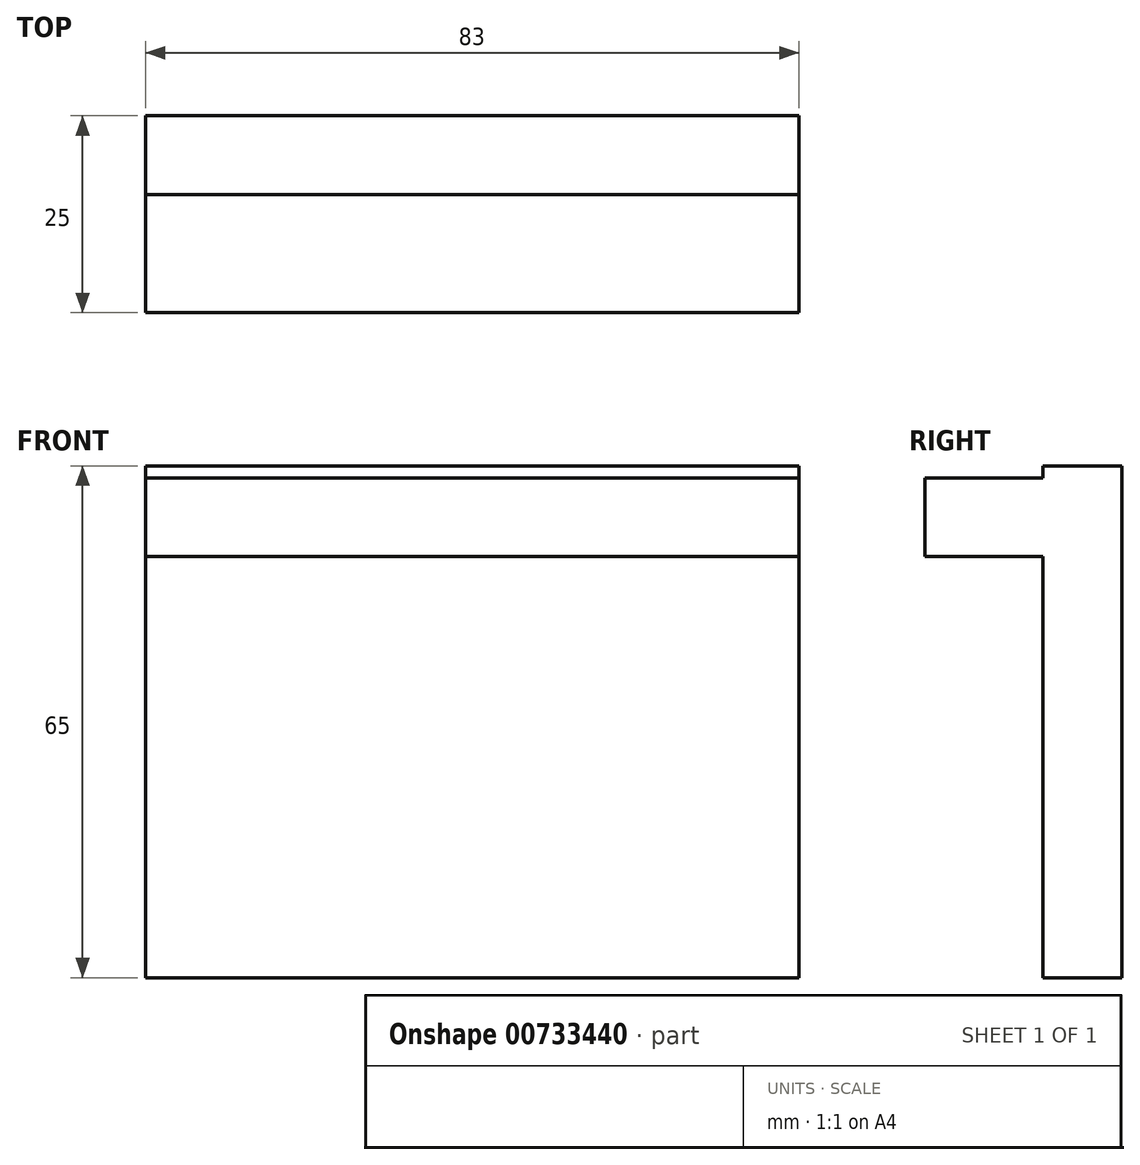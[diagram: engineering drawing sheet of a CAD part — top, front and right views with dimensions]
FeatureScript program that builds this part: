
annotation { "Feature Type Name" : "Feature", "Feature Type Description" : "" }
export const myFeature = defineFeature(function(context is Context, id is Id, definition is map)
    precondition{}
    {
        {
            var Q0;
            Q0=qCreatedBy(makeId("Top.planeOp"),FACE);
            var sketch = newSketch(context, id + "F0", { "sketchPlane" : qUnion([Q0])});
            skLineSegment(sketch, "E0.bottom", {"start": v(41.5, -5) * mm, "end": v(-41.5, -5) * mm});
            skLineSegment(sketch, "E0.top", {"start": v(41.5, 5) * mm, "end": v(-41.5, 5) * mm});
            skLineSegment(sketch, "E0.left", {"start": v(41.5, -5) * mm, "end": v(41.5, 5) * mm});
            skLineSegment(sketch, "E0.right", {"start": v(-41.5, -5) * mm, "end": v(-41.5, 5) * mm});
            skPoint(sketch, "E0.middle", {"position": v(0, 0) * mm});
            skSolve(sketch);
        }
        {
            var Q0;
            Q0=makeQuery(id+"F0.imprint","IMPRINT",FACE,{"disambiguationData":[TD([[makeQuery(id+"F0.imprint","IMPRINT",EDGE,{"derivedFrom":sQuery(id+"F0.wireOp",EDGE,"E0.bottom")}),-1.0]])]});
            var Q1;
            Q1 = qSketchRegion(id + "FKoPem74fLOwUCJ_1", true);
            extrude(context, id + "F1", {"entities" : qUnion([Q0, Q1]), "depth" : 65 * mm, "offsetDistance" : 25 * mm});
        }
        {
            var Q0;
            Q0=makeQuery(id+"F1.opExtrude","SWEPT_FACE",FACE,{"disambiguationData":[OSD([sQuery(id+"F0.wireOp",EDGE,"E0.bottom")])]});
            var sketch = newSketch(context, id + "F2", { "sketchPlane" : qUnion([Q0])});
            skLineSegment(sketch, "E1.bottom", {"start": v(-41.5, 63.5) * mm, "end": v(41.5, 63.5) * mm});
            skLineSegment(sketch, "E1.top", {"start": v(-41.5, 53.5) * mm, "end": v(41.5, 53.5) * mm});
            skLineSegment(sketch, "E1.left", {"start": v(-41.5, 63.5) * mm, "end": v(-41.5, 53.5) * mm});
            skLineSegment(sketch, "E1.right", {"start": v(41.5, 63.5) * mm, "end": v(41.5, 53.5) * mm});
            skSolve(sketch);
        }
        {
            var Q0;
            Q0 = qSketchRegion(id + "F2", true);
            extrude(context, id + "F3", {"entities" : qUnion([Q0]), "operationType" : NewBodyOperationType.ADD, "depth" : 15 * mm, "offsetDistance" : 25 * mm});
        }
    });
